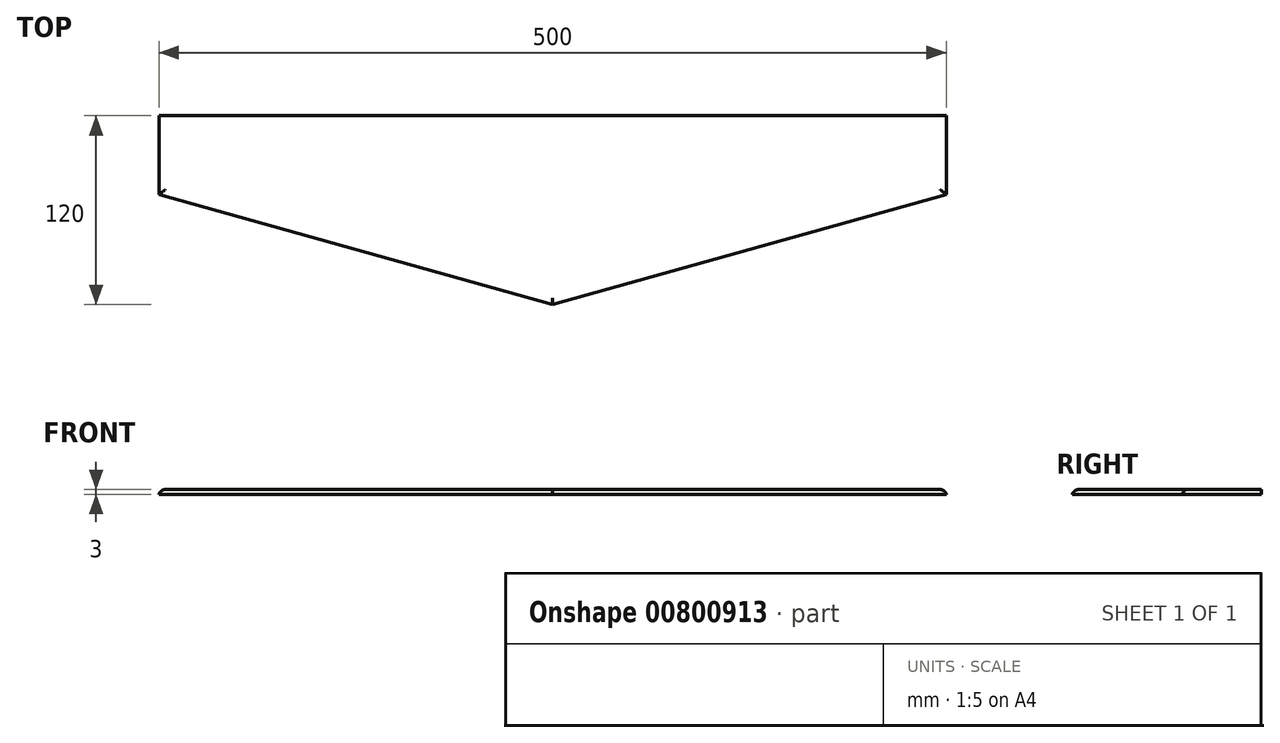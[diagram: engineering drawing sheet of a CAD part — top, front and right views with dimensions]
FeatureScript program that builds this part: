
annotation { "Feature Type Name" : "Feature", "Feature Type Description" : "" }
export const myFeature = defineFeature(function(context is Context, id is Id, definition is map)
    precondition{}
    {
        {
            var Q0;
            Q0=qCreatedBy(makeId("Top.planeOp"),FACE);
            var sketch = newSketch(context, id + "F0", { "sketchPlane" : qUnion([Q0])});
            skLineSegment(sketch, "E0", {"start": v(0, -60) * mm, "end": v(0, 60) * mm});
            skLineSegment(sketch, "E1", {"start": v(0, 60) * mm, "end": v(-250, 60) * mm});
            skLineSegment(sketch, "E2", {"start": v(-250, 60) * mm, "end": v(-250, 10) * mm});
            skLineSegment(sketch, "E3", {"start": v(-250, 10) * mm, "end": v(0, -60) * mm});
            skLineSegment(sketch, "E4.MirrorCS", {"start": v(0, 60) * mm, "end": v(250, 60) * mm});
            skLineSegment(sketch, "E5.MirrorCS", {"start": v(250, 60) * mm, "end": v(250, 10) * mm});
            skLineSegment(sketch, "E6.MirrorCS", {"start": v(250, 10) * mm, "end": v(0, -60) * mm});
            skSolve(sketch);
        }
        {
            var Q0;
            Q0 = qSketchRegion(id + "F0", true);
            extrude(context, id + "F1", {"entities" : qUnion([Q0]), "endBound" : BoundingType.SYMMETRIC, "depth" : 3 * mm, "offsetDistance" : 25 * mm});
        }
        {
            var Q0;
            Q0=makeQuery(id+"F1.opExtrude","CAP_EDGE",EDGE,{"disambiguationData":[OSD([sQuery(id+"F0.wireOp",EDGE,"E5.MirrorCS")])],"isStart":false});
            var Q1;
            Q1=makeQuery(id+"F1.opExtrude","CAP_EDGE",EDGE,{"disambiguationData":[OSD([sQuery(id+"F0.wireOp",EDGE,"E6.MirrorCS")])],"isStart":false});
            var Q2;
            Q2=makeQuery(id+"F1.opExtrude","CAP_EDGE",EDGE,{"disambiguationData":[OSD([sQuery(id+"F0.wireOp",EDGE,"E3")])],"isStart":false});
            var Q3;
            Q3=makeQuery(id+"F1.opExtrude","CAP_EDGE",EDGE,{"disambiguationData":[OSD([sQuery(id+"F0.wireOp",EDGE,"E2")])],"isStart":false});
            fillet(context, id + "F2", {"entities" : qUnion([Q0, Q1, Q2, Q3]), "radius" : 4 * mm, "tangentPropagation" : true, "allowEdgeOverflow" : false});
        }
    });
